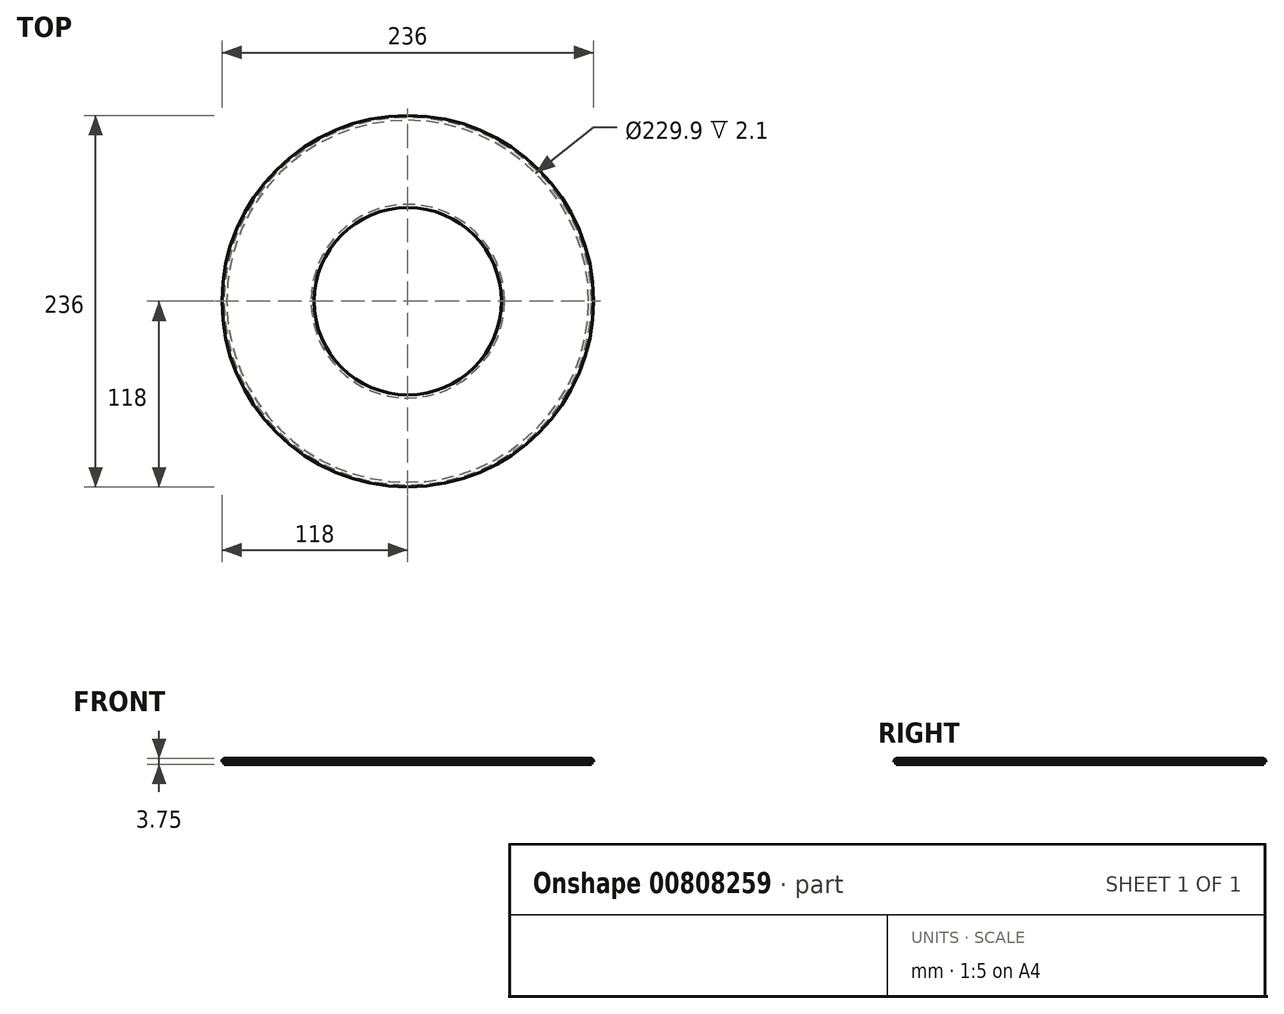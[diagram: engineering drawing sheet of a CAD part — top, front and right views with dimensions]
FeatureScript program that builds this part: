
annotation { "Feature Type Name" : "Feature", "Feature Type Description" : "" }
export const myFeature = defineFeature(function(context is Context, id is Id, definition is map)
    precondition{}
    {
        {
            var Q0;
            Q0=qCreatedBy(makeId("Front.planeOp"),FACE);
            var sketch = newSketch(context, id + "F0", { "sketchPlane" : qUnion([Q0])});
            skLineSegment(sketch, "E0", {"start": v(0, 0) * mm, "end": v(118, 0) * mm});
            skLineSegment(sketch, "E1", {"start": v(118, 0) * mm, "end": v(118, -2.25) * mm});
            skLineSegment(sketch, "E2", {"start": v(118, -2.25) * mm, "end": v(116.7, -2.25) * mm});
            skLineSegment(sketch, "E3", {"start": v(116.7, -2.25) * mm, "end": v(116.7, -3.75) * mm});
            skLineSegment(sketch, "E4", {"start": v(116.7, -3.75) * mm, "end": v(114.95, -3.75) * mm});
            skLineSegment(sketch, "E5", {"start": v(114.95, -3.75) * mm, "end": v(114.95, -1.65) * mm});
            skLineSegment(sketch, "E6", {"start": v(114.95, -1.65) * mm, "end": v(61.45, -1.65) * mm});
            skLineSegment(sketch, "E7", {"start": v(61.45, -1.65) * mm, "end": v(61.45, -1.75) * mm});
            skLineSegment(sketch, "E8", {"start": v(61.45, -1.75) * mm, "end": v(59.5, -1.75) * mm});
            skLineSegment(sketch, "E9", {"start": v(59.5, -1.75) * mm, "end": v(59.5, 0) * mm});
            skLineSegment(sketch, "E10", {"start": v(0, 26.56) * mm, "end": v(0, -31.38) * mm});
            skSolve(sketch);
        }
        {
            var Q0;
            {var subQ0=sQuery(id+"F0.wireOp",EDGE,"E1");Q0=makeQuery(id+"F0.imprint","IMPRINT",FACE,{"disambiguationData":[TD([[makeQuery(id+"F0.imprint","IMPRINT",EDGE,{"derivedFrom":subQ0}),-1.0]])]});}
            var Q1;
            Q1=sQuery(id+"F0.wireOp",EDGE,"E10");
            revolve(context, id + "F1", {"surfaceOperationType" : NewSurfaceOperationType.NEW, "entities" : qUnion([Q0]), "axis" : qUnion([Q1]), "revolveType" : RevolveType.FULL});
        }
        {
            var Q0;
            Q0=makeQuery(id+"F1.opRevolve","SWEPT_EDGE",EDGE,{"disambiguationData":[OSD([sQuery(id+"F0.wireOp",EDGE,"E0"),sQuery(id+"F0.wireOp",EDGE,"E9")])]});
            var Q1;
            Q1=makeQuery(id+"F1.opRevolve","SWEPT_EDGE",EDGE,{"disambiguationData":[OSD([sQuery(id+"F0.wireOp",EDGE,"E0"),sQuery(id+"F0.wireOp",EDGE,"E1")])]});
            fillet(context, id + "F2", {"entities" : qUnion([Q0, Q1]), "radius" : 1.8 * mm, "tangentPropagation" : true, "allowEdgeOverflow" : false});
        }
    });
